# Revit family: Prises non verrouilllées 100_130 V
name_source: partatom
category: Installations électriques
revit_build: Autodesk Revit 2018 (Build: 20170223_1515(x64)
units: mm (PartAtom-declared; Revit-internal decimal feet)

## family parameters
Conserver l'orientation des annotations = Non
Cote de connecteur circulaire = Utiliser le diamètre
Couper avec des vides une fois chargée = Non
Hôte = Face
Partagée = Non
Point de calcul de pièce = Non
Type d'élément = Normal

## types (4) — shared parameters
Couleur caractéristique = jaune
Elévation par défaut = 1000 mm  [stored 3.28084 ft]
Fabricant = Legrand
Famille produit = 0854-P17 TEMPRA PRO
Nombre de pôles = 3
Position de la Terre h = 4
Prise au standard international pour montage encastré ou saillie avec accessoire permet la connexion d'appareils de puissance = Prise au standard international pour montage encastré ou saillie avec accessoire permet la connexion d'appareils de puissance
Standard CEI ou NFC = CEI
Température maximum d'utilisation = 40
Température minimum d'installation = -5
Température minimum d'utilisation = -25
Tension V = 110 V  50/60 Hz  jaune
entraxe de fixation horizontal mm = 70 mm
entraxe de fixation vertical mm = 70 mm
hauteur mm = 84 mm  [stored 0.275591 ft]
installation Encastrée E ou Saillie S = encastré et saillie
largeur mm = 84 mm  [stored 0.275591 ft]
matériau du boitier = plastique
résistance aux chocs IK = 9
type de raccordement = bornes à vis

## per-type parameters (varying)
| type | Description | Intensité A | classe de protection IP | profondeur d'encastrement mm | profondeur mm | sans halogène |
| P17 - 32A - 2P+T - IP67 | LG-555481_Panneau de montage prise P17 32A 2P+T 100/130V IP67 | 32 A |  | 42 mm | 92 mm  [stored 0.301837 ft] | Non |
| P17 - 16A - 2P+T - IP67 | LG-555381_Panneau de montage prise P17 16A 2P+T 100/130V IP67 | 16 A | IP44 | 34 mm | 76 mm | Non |
| P17 - 32A - 2P+T - IP44 | LG-555281_Panneau de montage prise P17 32A 2P+T 100/130V IP44 | 32 A |  | 42 mm | 87 mm | Oui |
| P17 - 16A - 2P+T - IP44 | LG-555181_Panneau de montage prise P17 16A 2P+T 100/130V IP44 | 16 A | IP44 | 34 mm | 71 mm | Oui |

note: [stored X ft] marks values corroborated as IEEE doubles in the binary element streams (Revit-internal decimal feet)
